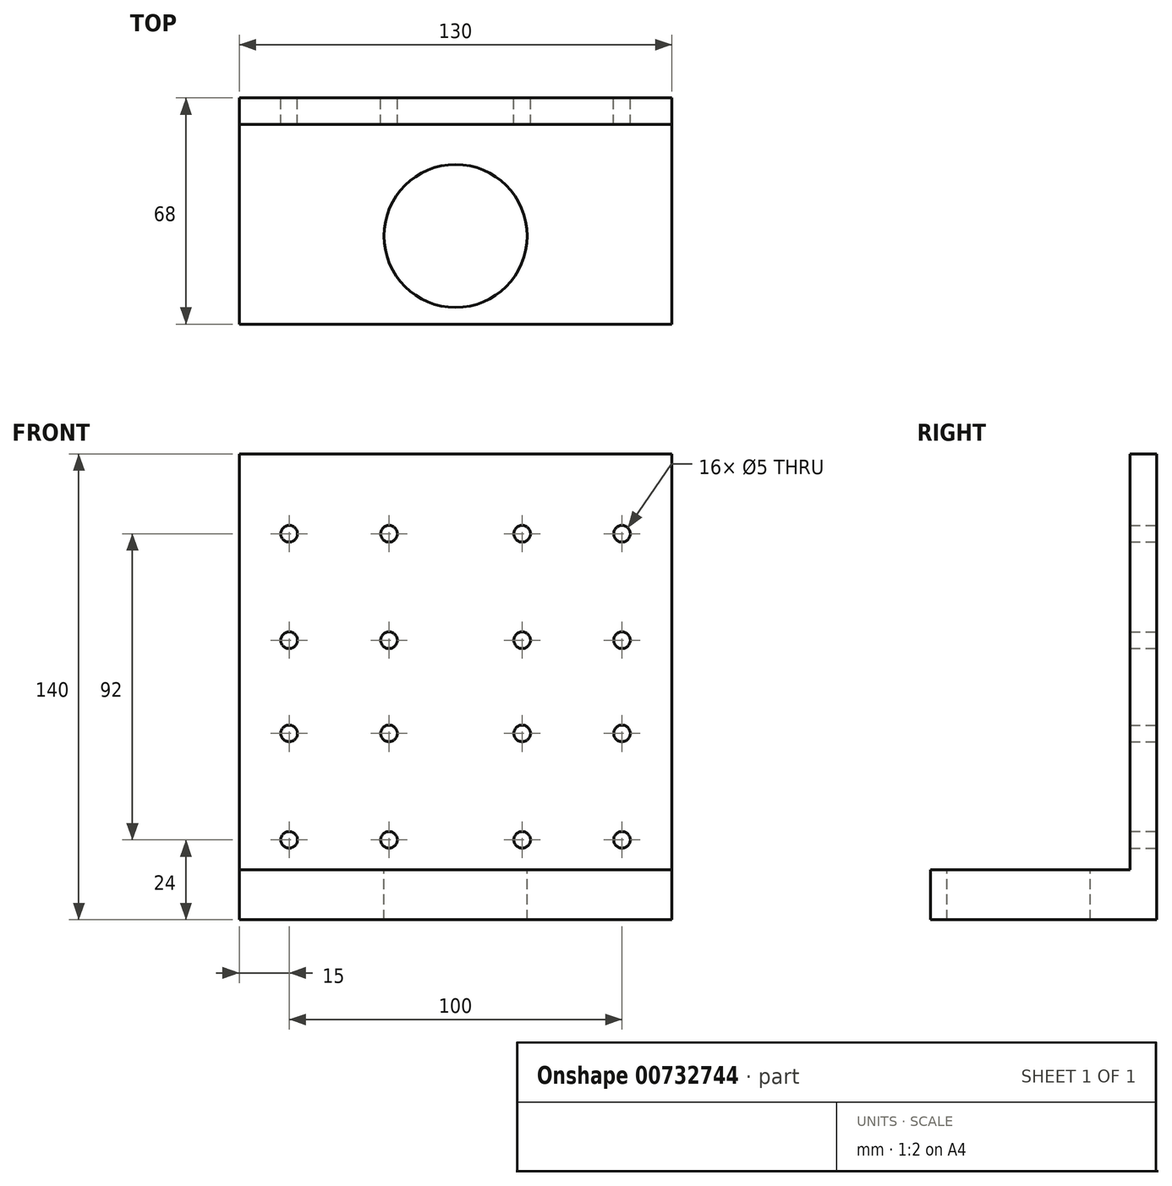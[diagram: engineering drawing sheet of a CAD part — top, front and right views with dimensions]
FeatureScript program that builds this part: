
annotation { "Feature Type Name" : "Feature", "Feature Type Description" : "" }
export const myFeature = defineFeature(function(context is Context, id is Id, definition is map)
    precondition{}
    {
        {
            var Q0;
            Q0=qCreatedBy(makeId("Front.planeOp"),FACE);
            var sketch = newSketch(context, id + "F0", { "sketchPlane" : qUnion([Q0])});
            skLineSegment(sketch, "E0.bottom", {"start": v(65, -70) * mm, "end": v(-65, -70) * mm});
            skLineSegment(sketch, "E0.top", {"start": v(65, 70) * mm, "end": v(-65, 70) * mm});
            skLineSegment(sketch, "E0.left", {"start": v(65, -70) * mm, "end": v(65, 70) * mm});
            skLineSegment(sketch, "E0.right", {"start": v(-65, -70) * mm, "end": v(-65, 70) * mm});
            skPoint(sketch, "E0.middle", {"position": v(0, 0) * mm});
            skLineSegment(sketch, "E1.bottom", {"start": v(-20, 14) * mm, "end": v(-50, 14) * mm, "construction": true});
            skLineSegment(sketch, "E1.top", {"start": v(-20, 46) * mm, "end": v(-50, 46) * mm, "construction": true});
            skLineSegment(sketch, "E1.left", {"start": v(-20, 14) * mm, "end": v(-20, 46) * mm, "construction": true});
            skLineSegment(sketch, "E1.right", {"start": v(-50, 14) * mm, "end": v(-50, 46) * mm, "construction": true});
            skPoint(sketch, "E1.middle", {"position": v(-35, 30) * mm});
            skCircle(sketch, "E2", {"center": v(-50, 46) * mm, "radius": 2.5 * mm});
            skCircle(sketch, "E3", {"center": v(-20, 46) * mm, "radius": 2.5 * mm});
            skCircle(sketch, "E4", {"center": v(-50, 14) * mm, "radius": 2.5 * mm});
            skCircle(sketch, "E5", {"center": v(-20, 14) * mm, "radius": 2.5 * mm});
            skCircle(sketch, "E6.MirrorC", {"center": v(20, 14) * mm, "radius": 2.5 * mm});
            skCircle(sketch, "E7.MirrorC", {"center": v(20, 46) * mm, "radius": 2.5 * mm});
            skCircle(sketch, "E8.MirrorC", {"center": v(50, 46) * mm, "radius": 2.5 * mm});
            skCircle(sketch, "E9.MirrorC", {"center": v(50, 14) * mm, "radius": 2.5 * mm});
            skCircle(sketch, "E10.MirrorC", {"center": v(-50, -14) * mm, "radius": 2.5 * mm});
            skCircle(sketch, "E11.MirrorC", {"center": v(-20, -14) * mm, "radius": 2.5 * mm});
            skCircle(sketch, "E12.MirrorC", {"center": v(20, -14) * mm, "radius": 2.5 * mm});
            skCircle(sketch, "E13.MirrorC", {"center": v(50, -14) * mm, "radius": 2.5 * mm});
            skCircle(sketch, "E14.MirrorC", {"center": v(50, -46) * mm, "radius": 2.5 * mm});
            skCircle(sketch, "E15.MirrorC", {"center": v(20, -46) * mm, "radius": 2.5 * mm});
            skCircle(sketch, "E16.MirrorC", {"center": v(-20, -46) * mm, "radius": 2.5 * mm});
            skCircle(sketch, "E17.MirrorC", {"center": v(-50, -46) * mm, "radius": 2.5 * mm});
            skSolve(sketch);
        }
        {
            var Q0;
            Q0 = qSketchRegion(id + "F0", true);
            extrude(context, id + "F1", {"entities" : qUnion([Q0]), "depth" : 8 * mm, "offsetDistance" : 25 * mm});
        }
        {
            var Q0;
            Q0=makeQuery(id+"F1.opExtrude","CAP_FACE",FACE,{"disambiguationData":[OSD([sQuery(id+"F0.wireOp",EDGE,"E0.bottom"),sQuery(id+"F0.wireOp",EDGE,"E0.top"),sQuery(id+"F0.wireOp",EDGE,"E0.left"),sQuery(id+"F0.wireOp",EDGE,"E0.right"),sQuery(id+"F0.wireOp",EDGE,"E2"),sQuery(id+"F0.wireOp",EDGE,"E3"),sQuery(id+"F0.wireOp",EDGE,"E4"),sQuery(id+"F0.wireOp",EDGE,"E5"),sQuery(id+"F0.wireOp",EDGE,"E6.MirrorC"),sQuery(id+"F0.wireOp",EDGE,"E7.MirrorC"),sQuery(id+"F0.wireOp",EDGE,"E8.MirrorC"),sQuery(id+"F0.wireOp",EDGE,"E9.MirrorC"),sQuery(id+"F0.wireOp",EDGE,"E10.MirrorC"),sQuery(id+"F0.wireOp",EDGE,"E11.MirrorC"),sQuery(id+"F0.wireOp",EDGE,"E12.MirrorC"),sQuery(id+"F0.wireOp",EDGE,"E13.MirrorC"),sQuery(id+"F0.wireOp",EDGE,"E14.MirrorC"),sQuery(id+"F0.wireOp",EDGE,"E15.MirrorC"),sQuery(id+"F0.wireOp",EDGE,"E16.MirrorC"),sQuery(id+"F0.wireOp",EDGE,"E17.MirrorC")])],"isStart":false});
            var sketch = newSketch(context, id + "F2", { "sketchPlane" : qUnion([Q0])});
            skLineSegment(sketch, "E18.bottom", {"start": v(-65, -70) * mm, "end": v(65, -70) * mm});
            skLineSegment(sketch, "E18.top", {"start": v(-65, -55) * mm, "end": v(65, -55) * mm});
            skLineSegment(sketch, "E18.left", {"start": v(-65, -70) * mm, "end": v(-65, -55) * mm});
            skLineSegment(sketch, "E18.right", {"start": v(65, -70) * mm, "end": v(65, -55) * mm});
            skSolve(sketch);
        }
        {
            var Q0;
            Q0 = qSketchRegion(id + "F2", true);
            extrude(context, id + "F3", {"entities" : qUnion([Q0]), "operationType" : NewBodyOperationType.ADD, "depth" : 60 * mm, "offsetDistance" : 25 * mm});
        }
        {
            var Q0;
            Q0=makeQuery(id+"F3.opExtrude","SWEPT_FACE",FACE,{"disambiguationData":[OSD([sQuery(id+"F2.wireOp",EDGE,"E18.top")])]});
            var sketch = newSketch(context, id + "F4", { "sketchPlane" : qUnion([Q0])});
            skLineSegment(sketch, "E19", {"start": v(0, -8) * mm, "end": v(0, -68) * mm, "construction": true});
            skCircle(sketch, "E20", {"center": v(0, -41.5) * mm, "radius": 21.5 * mm});
            skSolve(sketch);
        }
        {
            var Q0;
            Q0 = qSketchRegion(id + "F4", true);
            extrude(context, id + "F5", {"entities" : qUnion([Q0]), "operationType" : NewBodyOperationType.REMOVE, "oppositeDirection" : true, "depth" : 25 * mm, "offsetDistance" : 25 * mm});
        }
    });
